# Revit family: Toilet_Elongated-Right_Height-American_Standard-Clean_Siphonic-3381.216
name_source: partatom
category: Plumbing Fixtures
revit_build: Autodesk Revit 2014 (Build: 20130308_1515(x64)
units: mm (PartAtom-declared; Revit-internal decimal feet)

## types (2) — shared parameters
Assembly Code = D2010110
Bowl Shape = Elongated
CW Connection = Yes
CWFU = 5
Cold Water Connection Diameter = 1/2"
Cold Water Connection Radius = 1/4"
Default Elevation = 0"
HW Connection = No
Installation Type = Floor Mounted
Length = 29 3/4"
Manufacturer = American Standard
Material = Vitreous China-American Standard-020-White
Price = Prices may vary. Please consult Manufacturer Representative for most up-to-date price list.
Product Documentation Link = https://www.americanstandard-us.com
Product Page URL = https://www.americanstandard-us.com
Revised Date = 02/22/2017
URL = http://www.americanstandard-us.com
Vent Connection = No
WFU = 5
Warranty Information = 5 Years Limited
Waste Connection = Yes
Waste Connection Diameter = 2"
Waste Connection Radius = 1"
Width = 15"
zero-valued in all types: HWFU

## per-type parameters (varying)
| type | Aquaguard Liner | Description | Flush Rate | Height |
| 2887.218 | No | H2Option Siphonic Dual Flush Elongated Toilet. | (4.8 Lpf/1.28gpf) or (3.4 Lpf/0.92 gpf) | 30" |
| 3381.216 | Yes | Clean Siphonic Dual Flush Right Height Elongated Complete Toilet | (6.0 Lpf/1.6gpf) or (3.8 Lpf/1.0 gpf) | 31" |

note: column(s) folded — value = type name in every type: Model

## geometry (parser evidence)
native form markers: Sweep x1
no freeform markers — native parametric forms only
